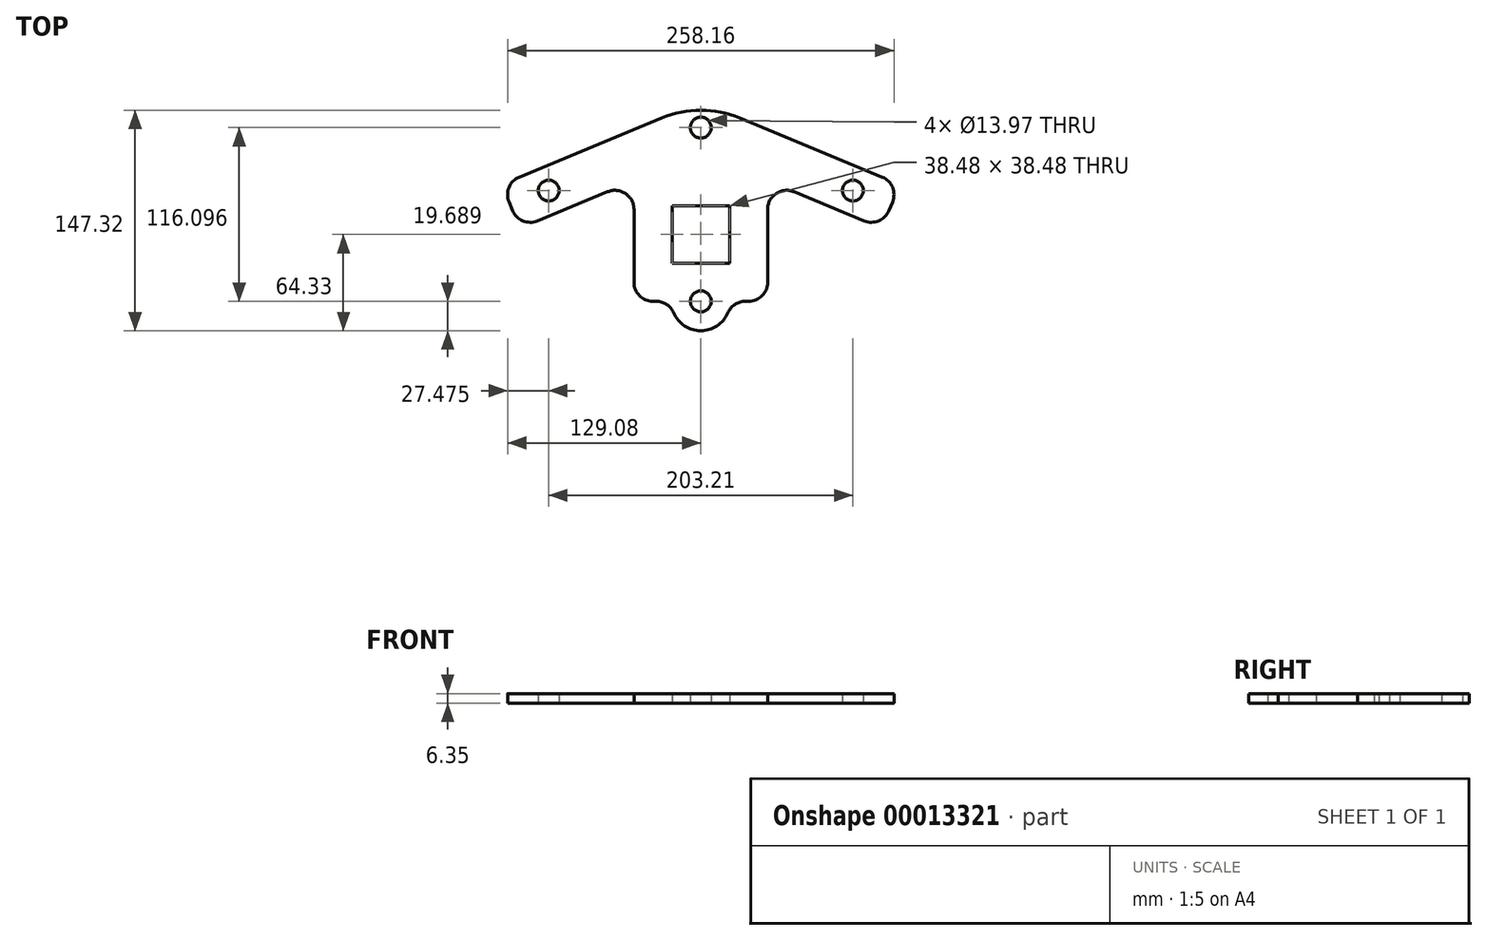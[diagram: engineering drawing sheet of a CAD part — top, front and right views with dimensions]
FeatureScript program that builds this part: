
annotation { "Feature Type Name" : "Feature", "Feature Type Description" : "" }
export const myFeature = defineFeature(function(context is Context, id is Id, definition is map)
    precondition{}
    {
        {
            var Q0;
            Q0=qCreatedBy(makeId("Top.planeOp"),FACE);
            var sketch = newSketch(context, id + "F0", { "sketchPlane" : qUnion([Q0])});
            skPoint(sketch, "E0.rect.middle", {"position": v(0, 0) * mm});
            skLineSegment(sketch, "E1.2", {"start": v(-44.64, 16.83) * mm, "end": v(-44.64, -31.94) * mm});
            skCircle(sketch, "E2", {"center": v(0, -44.64) * mm, "radius": 6.99 * mm});
            skArc(sketch, "E3.0", {"start": v(-18.1, -52.36) * mm, "mid": v(-10.85, -61.06) * mm, "end": v(0, -64.33) * mm});
            skLineSegment(sketch, "E4.trimOffspring", {"start": v(-29.8, -44.64) * mm, "end": v(-31.94, -44.64) * mm});
            skLineSegment(sketch, "E5", {"start": v(0, -64.33) * mm, "end": v(0, 148.4) * mm, "construction": true});
            skLineSegment(sketch, "E6.0.MirrorCS", {"start": v(-25.95, 77.83) * mm, "end": v(-121.24, 38.36) * mm});
            skLineSegment(sketch, "E7.0.MirrorCS", {"start": v(-128.11, 21.77) * mm, "end": v(-125.73, 16) * mm});
            skCircle(sketch, "E8.0.MirrorC", {"center": v(-101.6, 29.37) * mm, "radius": 6.99 * mm});
            skLineSegment(sketch, "E9.0.MirrorCS", {"start": v(-109.13, 9.13) * mm, "end": v(-62.2, 28.57) * mm});
            skArc(sketch, "E10.filletArc", {"start": v(-44.64, 16.83) * mm, "mid": v(-50.28, 27.4) * mm, "end": v(-62.2, 28.57) * mm});
            skPoint(sketch, "E11.visualSharp", {"position": v(0, 88.58) * mm});
            skArc(sketch, "E12.filletArc", {"start": v(-121.24, 38.36) * mm, "mid": v(-128.11, 31.49) * mm, "end": v(-128.11, 21.77) * mm});
            skArc(sketch, "E13.filletArc", {"start": v(-125.73, 16) * mm, "mid": v(-118.85, 9.13) * mm, "end": v(-109.13, 9.13) * mm});
            skArc(sketch, "E14.filletArc", {"start": v(-44.64, -31.94) * mm, "mid": v(-40.92, -40.92) * mm, "end": v(-31.94, -44.64) * mm});
            skArc(sketch, "E15.filletArc", {"start": v(-18.1, -52.36) * mm, "mid": v(-22.79, -46.74) * mm, "end": v(-29.8, -44.64) * mm});
            skLineSegment(sketch, "E16.rect.bottom", {"start": v(19.24, 19.24) * mm, "end": v(-19.24, 19.24) * mm});
            skLineSegment(sketch, "E16.rect.top", {"start": v(19.24, -19.24) * mm, "end": v(-19.24, -19.24) * mm});
            skLineSegment(sketch, "E16.rect.left", {"start": v(19.24, 19.24) * mm, "end": v(19.24, -19.24) * mm});
            skLineSegment(sketch, "E16.rect.right", {"start": v(-19.24, 19.24) * mm, "end": v(-19.24, -19.24) * mm});
            skCircle(sketch, "E17", {"center": v(0, 71.46) * mm, "radius": 6.99 * mm});
            skLineSegment(sketch, "E18", {"start": v(0, 51.82) * mm, "end": v(24.35, 51.82) * mm, "construction": true});
            skCircle(sketch, "E19.5.MirrorC", {"center": v(0, 148.27) * mm, "radius": 6.99 * mm, "construction": true});
            skPoint(sketch, "E20.visualSharp", {"position": v(-44.64, 70.09) * mm});
            skLineSegment(sketch, "E21", {"start": v(0, 71.46) * mm, "end": v(-101.6, 29.37) * mm, "construction": true});
            skLineSegment(sketch, "E22", {"start": v(-101.6, 29.37) * mm, "end": v(-126.92, 18.88) * mm, "construction": true});
            skLineSegment(sketch, "E23", {"start": v(-18.1, 148.27) * mm, "end": v(-18.1, 89.56) * mm, "construction": true});
            skPoint(sketch, "E24.visualSharp", {"position": v(-18.1, 81.08) * mm});
            skArc(sketch, "E24.filletArc", {"start": v(-25.95, 77.83) * mm, "mid": v(-20.25, 82.5) * mm, "end": v(-18.1, 89.56) * mm, "construction": true});
            skArc(sketch, "E25", {"start": v(0, 166.38) * mm, "mid": v(-12.8, 161.08) * mm, "end": v(-18.1, 148.27) * mm, "construction": true});
            skLineSegment(sketch, "E26.1.MirrorCS", {"start": v(29.8, -44.64) * mm, "end": v(31.94, -44.64) * mm});
            skLineSegment(sketch, "E26.2.MirrorCS", {"start": v(128.11, 21.77) * mm, "end": v(125.73, 16) * mm});
            skArc(sketch, "E26.3.MirrorCS", {"start": v(25.95, 77.83) * mm, "mid": v(20.25, 82.5) * mm, "end": v(18.1, 89.56) * mm, "construction": true});
            skArc(sketch, "E26.5.MirrorCS", {"start": v(44.64, -31.94) * mm, "mid": v(40.92, -40.92) * mm, "end": v(31.94, -44.64) * mm});
            skLineSegment(sketch, "E26.6.MirrorCS", {"start": v(25.95, 77.83) * mm, "end": v(121.24, 38.36) * mm});
            skLineSegment(sketch, "E26.7.MirrorCS", {"start": v(109.13, 9.13) * mm, "end": v(62.2, 28.57) * mm});
            skPoint(sketch, "E26.8.MirrorP", {"position": v(44.64, 70.09) * mm});
            skLineSegment(sketch, "E26.9.MirrorCS", {"start": v(18.1, 148.27) * mm, "end": v(18.1, 89.56) * mm, "construction": true});
            skLineSegment(sketch, "E26.10.MirrorCS", {"start": v(44.64, 16.83) * mm, "end": v(44.64, -31.94) * mm});
            skArc(sketch, "E26.11.MirrorCS", {"start": v(121.24, 38.36) * mm, "mid": v(128.11, 31.49) * mm, "end": v(128.11, 21.77) * mm});
            skArc(sketch, "E26.12.MirrorCS", {"start": v(18.1, -52.36) * mm, "mid": v(10.85, -61.06) * mm, "end": v(0, -64.33) * mm});
            skArc(sketch, "E26.13.MirrorCS", {"start": v(44.64, 16.83) * mm, "mid": v(50.28, 27.4) * mm, "end": v(62.2, 28.57) * mm});
            skArc(sketch, "E26.14.MirrorCS", {"start": v(125.73, 16) * mm, "mid": v(118.85, 9.13) * mm, "end": v(109.13, 9.13) * mm});
            skPoint(sketch, "E26.15.MirrorP", {"position": v(18.1, 81.08) * mm});
            skCircle(sketch, "E26.16.MirrorC", {"center": v(101.6, 29.37) * mm, "radius": 6.99 * mm});
            skArc(sketch, "E26.17.MirrorCS", {"start": v(0, 166.38) * mm, "mid": v(12.8, 161.08) * mm, "end": v(18.1, 148.27) * mm, "construction": true});
            skArc(sketch, "E26.18.MirrorCS", {"start": v(18.1, -52.36) * mm, "mid": v(22.79, -46.74) * mm, "end": v(29.8, -44.64) * mm});
            skArc(sketch, "E27", {"start": v(-25.95, 77.83) * mm, "mid": v(0, 83) * mm, "end": v(25.95, 77.83) * mm});
            skSolve(sketch);
        }
        {
            var Q0;
            Q0 = qSketchRegion(id + "F0", true);
            extrude(context, id + "F1", {"entities" : qUnion([Q0]), "depth" : 6.35 * mm});
        }
    });
